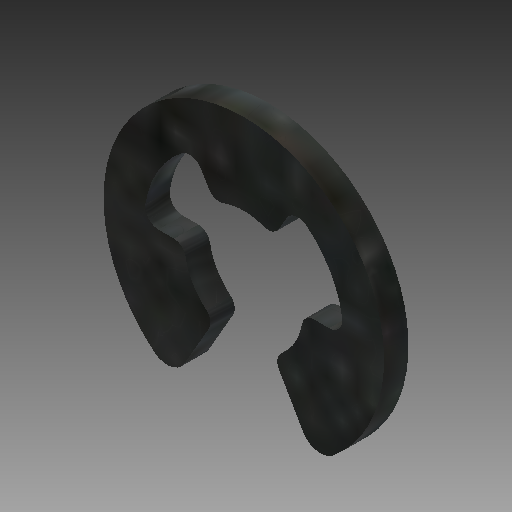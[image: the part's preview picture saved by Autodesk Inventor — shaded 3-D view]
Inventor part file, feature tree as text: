
AUTODESK INVENTOR PART (.ipt)
format: ipt  version: 2017 (Build 210142000, 142)  size: 175,616 bytes
history: native  units: in
note: dims shown in document units (in); Inventor stores cm internally (conversion verified against a paired STEP export)
features: other x7, extrude x1, sketch x1
ambient origin geometry x8: Origin, YZ Plane, XZ Plane, XY Plane, X Axis, Y Axis, Z Axis, Center Point
bodies: Solid1 (feature_tree)
feature tree (9):
  extrude  "Extrusion1"  [1 undecoded]
  other  "RR_XY"
  other  "RR_YZ"
  other  "RR_ZX"
  other  "RR_X"
  other  "RR_Y"
  other  "RR_Z"
  other  "RR_Center"
  sketch  "Sketch_1"  dims[d0=0.0435in d1=0.0in]
note: 1 required parameter value undecoded (feature->parameter linkage not recoverable at this tier; creation-order binding heuristic only, values carry confidence <= 0.55)
